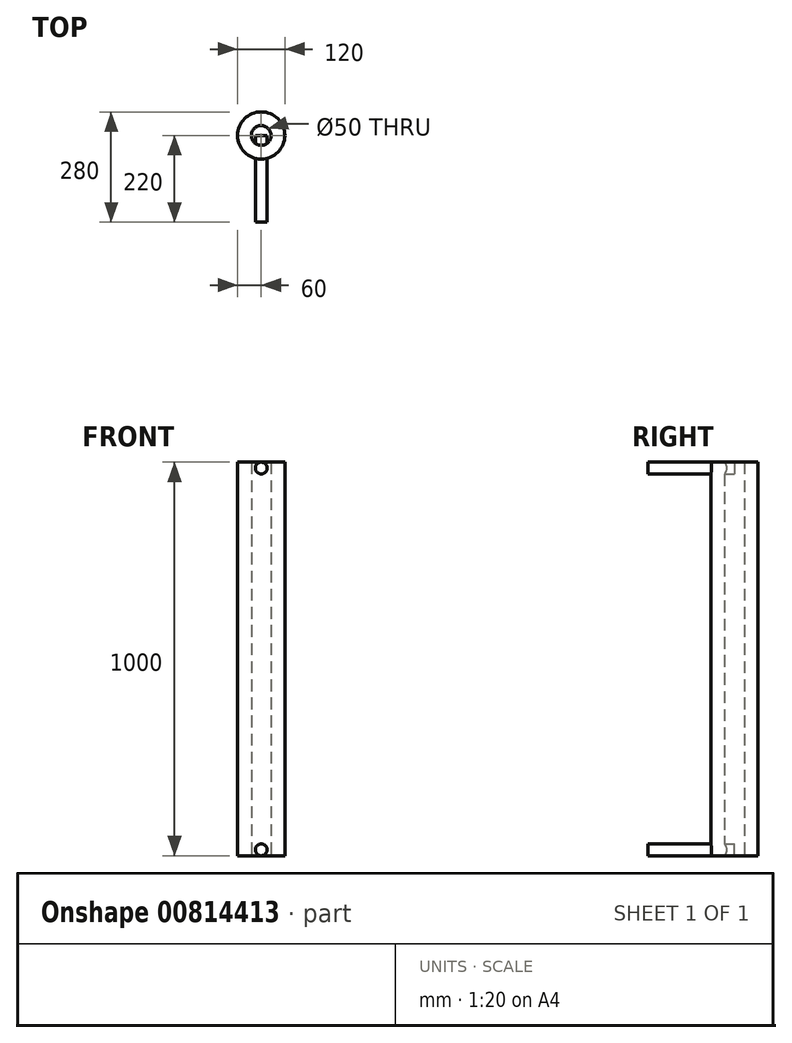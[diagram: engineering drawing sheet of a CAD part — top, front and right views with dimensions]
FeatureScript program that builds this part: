
annotation { "Feature Type Name" : "Feature", "Feature Type Description" : "" }
export const myFeature = defineFeature(function(context is Context, id is Id, definition is map)
    precondition{}
    {
        {
            var Q0;
            Q0=qCreatedBy(makeId("Top.planeOp"),FACE);
            var sketch = newSketch(context, id + "F0", { "sketchPlane" : qUnion([Q0])});
            skCircle(sketch, "E0", {"center": v(0, 0) * mm, "radius": 60 * mm});
            skCircle(sketch, "E1", {"center": v(0, 0) * mm, "radius": 25 * mm});
            skSolve(sketch);
        }
        {
            var Q0;
            Q0=makeQuery(id+"F0.imprint","IMPRINT",FACE,{"disambiguationData":[TD([[makeQuery(id+"F0.imprint","IMPRINT",EDGE,{"derivedFrom":sQuery(id+"F0.wireOp",EDGE,"E0")}),1.0]])]});
            extrude(context, id + "F1", {"entities" : qUnion([Q0]), "depth" : 1000 * mm, "offsetDistance" : 25 * mm});
        }
        {
            var Q0;
            Q0=qCreatedBy(makeId("Front.planeOp"),FACE);
            var sketch = newSketch(context, id + "F2", { "sketchPlane" : qUnion([Q0])});
            skPoint(sketch, "E2", {"position": v(0, 15) * mm});
            skCircle(sketch, "E3", {"center": v(0, 15) * mm, "radius": 15 * mm});
            skSolve(sketch);
        }
        {
            var Q0;
            Q0 = qSketchRegion(id + "F2", true);
            extrude(context, id + "F3", {"entities" : qUnion([Q0]), "operationType" : NewBodyOperationType.ADD, "depth" : 220 * mm, "offsetDistance" : 25 * mm});
        }
        {
            var Q0;
            Q0=qCreatedBy(makeId("Front.planeOp"),FACE);
            var sketch = newSketch(context, id + "F4", { "sketchPlane" : qUnion([Q0])});
            skPoint(sketch, "E4", {"position": v(0, 0) * mm});
            skPoint(sketch, "E5", {"position": v(0, 985) * mm});
            skCircle(sketch, "E6", {"center": v(0, 985) * mm, "radius": 15 * mm});
            skSolve(sketch);
        }
        {
            var Q0;
            Q0 = qSketchRegion(id + "F4", true);
            extrude(context, id + "F5", {"entities" : qUnion([Q0]), "operationType" : NewBodyOperationType.ADD, "depth" : 220 * mm, "offsetDistance" : 25 * mm});
        }
    });
